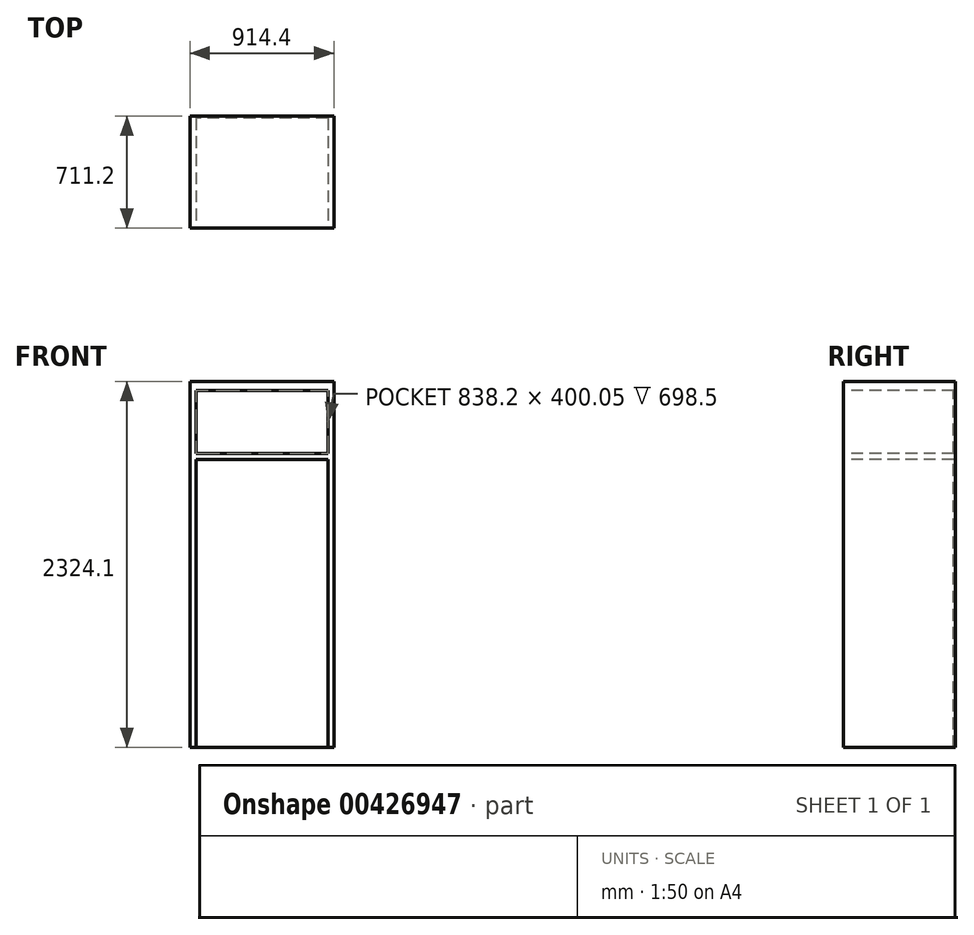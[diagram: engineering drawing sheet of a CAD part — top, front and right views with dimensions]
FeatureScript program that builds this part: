
annotation { "Feature Type Name" : "Feature", "Feature Type Description" : "" }
export const myFeature = defineFeature(function(context is Context, id is Id, definition is map)
    precondition{}
    {
        {
            var Q0;
            Q0=qCreatedBy(makeId("Right.planeOp"),FACE);
            var sketch = newSketch(context, id + "F0", { "sketchPlane" : qUnion([Q0])});
            skLineSegment(sketch, "E0.bottom", {"start": v(0, 0) * mm, "end": v(-711.2, 0) * mm});
            skLineSegment(sketch, "E0.top", {"start": v(0, 2324.1) * mm, "end": v(-711.2, 2324.1) * mm});
            skLineSegment(sketch, "E0.left", {"start": v(0, 0) * mm, "end": v(0, 2324.1) * mm});
            skLineSegment(sketch, "E0.right", {"start": v(-711.2, 0) * mm, "end": v(-711.2, 2324.1) * mm});
            skSolve(sketch);
        }
        {
            var Q0;
            Q0=makeQuery(id+"F0.imprint","IMPRINT",FACE,{"disambiguationData":[TD([[makeQuery(id+"F0.imprint","IMPRINT",EDGE,{"derivedFrom":sQuery(id+"F0.wireOp",EDGE,"E0.bottom")}),-1.0]])]});
            extrude(context, id + "F1", {"entities" : qUnion([Q0]), "depth" : 914.4 * mm});
        }
        {
            var Q0;
            Q0=makeQuery(id+"F1.opExtrude","SWEPT_FACE",FACE,{"disambiguationData":[OSD([sQuery(id+"F0.wireOp",EDGE,"E0.right")])]});
            var sketch = newSketch(context, id + "F2", { "sketchPlane" : qUnion([Q0])});
            skLineSegment(sketch, "E1.bottom", {"start": v(38.1, 0) * mm, "end": v(876.3, 0) * mm});
            skLineSegment(sketch, "E1.top", {"start": v(38.1, 1828.8) * mm, "end": v(876.3, 1828.8) * mm});
            skLineSegment(sketch, "E1.left", {"start": v(38.1, 0) * mm, "end": v(38.1, 1828.8) * mm});
            skLineSegment(sketch, "E1.right", {"start": v(876.3, 0) * mm, "end": v(876.3, 1828.8) * mm});
            skLineSegment(sketch, "E2.bottom", {"start": v(38.1, 1866.9) * mm, "end": v(876.3, 1866.9) * mm});
            skLineSegment(sketch, "E2.top", {"start": v(38.1, 2266.95) * mm, "end": v(876.3, 2266.95) * mm});
            skLineSegment(sketch, "E2.left", {"start": v(38.1, 1866.9) * mm, "end": v(38.1, 2266.95) * mm});
            skLineSegment(sketch, "E2.right", {"start": v(876.3, 1866.9) * mm, "end": v(876.3, 2266.95) * mm});
            skSolve(sketch);
        }
        {
            var Q0;
            Q0=makeQuery(id+"F2.imprint","IMPRINT",FACE,{"disambiguationData":[TD([[makeQuery(id+"F2.imprint","IMPRINT",EDGE,{"derivedFrom":sQuery(id+"F2.wireOp",EDGE,"E1.bottom")}),-1.0]])]});
            var Q1;
            Q1=makeQuery(id+"F2.imprint","IMPRINT",FACE,{"disambiguationData":[TD([[makeQuery(id+"F2.imprint","IMPRINT",EDGE,{"derivedFrom":sQuery(id+"F2.wireOp",EDGE,"E2.bottom")}),1.0]])]});
            extrude(context, id + "F3", {"entities" : qUnion([Q0, Q1]), "operationType" : NewBodyOperationType.REMOVE, "oppositeDirection" : true, "depth" : 698.5 * mm});
        }
    });
